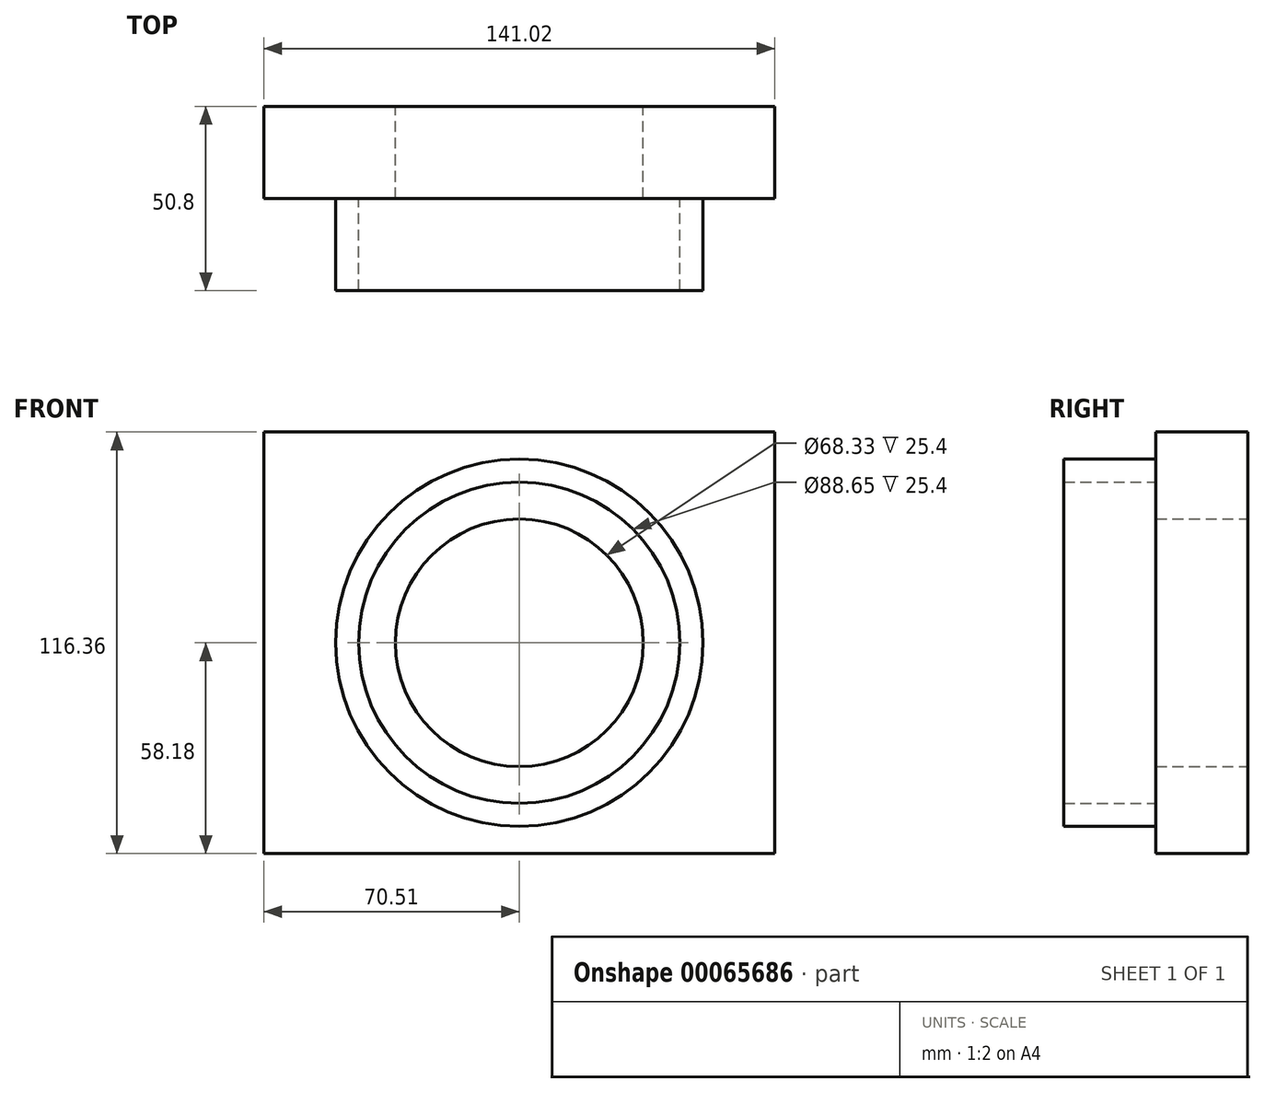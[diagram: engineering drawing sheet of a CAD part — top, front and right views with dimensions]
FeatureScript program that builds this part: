
annotation { "Feature Type Name" : "Feature", "Feature Type Description" : "" }
export const myFeature = defineFeature(function(context is Context, id is Id, definition is map)
    precondition{}
    {
        {
            var Q0;
            Q0=qCreatedBy(makeId("Front.planeOp"),FACE);
            var sketch = newSketch(context, id + "F0", { "sketchPlane" : qUnion([Q0])});
            skLineSegment(sketch, "E0.rect.bottom", {"start": v(-70.51, 58.18) * mm, "end": v(70.51, 58.18) * mm});
            skLineSegment(sketch, "E0.rect.top", {"start": v(-70.51, -58.18) * mm, "end": v(70.51, -58.18) * mm});
            skLineSegment(sketch, "E0.rect.left", {"start": v(-70.51, 58.18) * mm, "end": v(-70.51, -58.18) * mm});
            skLineSegment(sketch, "E0.rect.right", {"start": v(70.51, 58.18) * mm, "end": v(70.51, -58.18) * mm});
            skPoint(sketch, "E0.rect.middle", {"position": v(0, 0) * mm});
            skCircle(sketch, "E1", {"center": v(0, 0) * mm, "radius": 34.17 * mm});
            skSolve(sketch);
        }
        {
            var Q0;
            Q0 = qSketchRegion(id + "F0", true);
            extrude(context, id + "F1", {"entities" : qUnion([Q0]), "depth" : 25.4 * mm});
        }
        {
            var Q0;
            Q0=makeQuery(id+"F1.opExtrude","CAP_FACE",FACE,{"disambiguationData":[OSD([sQuery(id+"F0.wireOp",EDGE,"E0.rect.bottom"),sQuery(id+"F0.wireOp",EDGE,"E0.rect.top"),sQuery(id+"F0.wireOp",EDGE,"E0.rect.left"),sQuery(id+"F0.wireOp",EDGE,"E0.rect.right"),sQuery(id+"F0.wireOp",EDGE,"E1")])],"isStart":false});
            var sketch = newSketch(context, id + "F2", { "sketchPlane" : qUnion([Q0])});
            skCircle(sketch, "E2.0", {"center": v(0, 0) * mm, "radius": 34.17 * mm});
            skCircle(sketch, "E3.0", {"center": v(0, 0) * mm, "radius": 23.73 * mm});
            skCircle(sketch, "E4.0", {"center": v(0, 0) * mm, "radius": 44.33 * mm});
            skCircle(sketch, "E5.0", {"center": v(0, 0) * mm, "radius": 50.68 * mm});
            skSolve(sketch);
        }
        {
            var Q0;
            Q0 = qSketchRegion(id + "F2", true);
            extrude(context, id + "F3", {"entities" : qUnion([Q0]), "operationType" : NewBodyOperationType.ADD, "depth" : 25.4 * mm});
        }
    });
